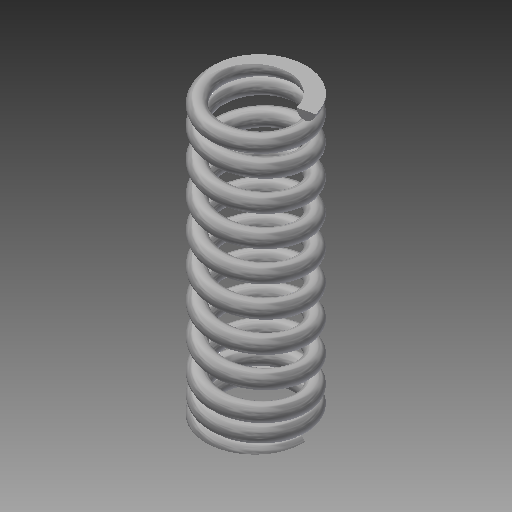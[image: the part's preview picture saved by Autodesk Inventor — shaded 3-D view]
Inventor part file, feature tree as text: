
AUTODESK INVENTOR PART (.ipt)
format: ipt  version: 2019 (Build 230136000, 136)  size: 1,027,072 bytes
history: native  units: mm
features: other x67, extrude x8, helix x5, sketch x3, sweep x2, plane x1
ambient origin geometry x8: Origin, YZ Plane, XZ Plane, XY Plane, X Axis, Y Axis, Z Axis, Center Point
bodies: Solid1 (feature_tree)
feature tree (86):
  other  "Main Coil Path(Right)"
  other  "Section Work Plane(Right)"
  other  "Start Work Plane(Right)"
  other  "End Work Plane(Right)"
  other  "End Cut Work Plane(Right)"
  other  "Start Cut Work Plane(Right)"
  other  "Plain Ends Cut Work Plane 1(Right)"
  other  "Plain Ends Cut Work Plane 2(Right)"
  sweep  "Main Coil Feature(R)"
  other  "Start Transition Coil 1(Right)"
  helix  "Coil  Start Transition 2(R)"  [1 undecoded]
  helix  "Coil  Start Transition 3(R)"  [1 undecoded]
  helix  "Coil  Start Transition 4(R)"  [1 undecoded]
  other  "Start Ends Coil(Right)"
  extrude  "Start Cut Feature(Right)"  Depth=10.0mm
  other  "End Transition Coil 1(Right)"
  other  "End Transition Coil 2(Right)"
  other  "End Transition Coil 3(Right)"
  other  "End Transition Coil 4(Right)"
  other  "End Coil(Right)"
  extrude  "End Cut Feature(Right)"  Depth=10.0mm
  extrude  "Plain Ends Cut Feature 1(Right)"  Depth=10.0mm
  extrude  "Plain Ends Cut  2(R)"  Depth=10.0mm TaperAngle=0.0deg
  other  "Main Coil Path(Left)"
  other  "Section Work Plane(Left)"
  other  "Start Work Plane(Left)"
  other  "End Work Plane(Left)"
  other  "End Cut Work Plane(Left)"
  other  "Start Cut Work Plane(Left)"
  other  "Plain Ends Cut Work Plane 1(Left)"
  other  "Plain Ends Cut Work Plane 2(Left)"
  sweep  "Main Coil Feature(L)"
  other  "Start Transition Coil 1(Left)"
  other  "Start Transition Coil 2(Left)"
  other  "Start Transition Coil 3(Left)"
  other  "Start Transition Coil 4(Left)"
  other  "Start Ends Coil(Left)"
  extrude  "Start Cut Feature(Left)"  Depth=10.0mm TaperAngle=0.0deg
  other  "End Transition Coil 1(Left)"
  other  "End Transition Coil 2(Left)"
  other  "End Transition Coil 3(Left)"
  other  "End Transition Coil 4(Left)"
  other  "End Coil(Left)"
  extrude  "End Cut Feature(Left)"  Depth=10.0mm
  extrude  "Cut Plain Ends Cut 1(L)"  Depth=10.0mm
  extrude  "Cut Plain Ends Cut 2(L)"  Depth=10.0mm
  other  "iMate Based Work Plane"
  other  "Preview Center Point"
  other  "Preview X Axis"
  other  "Path Section Sketch(Right)"
  other  "Srf1"
  helix  "Coil Section Sketch(Right)"  [1 undecoded]
  other  "Start Transition Coil Sketch 1(Right)"
  sketch  "Sketch  Start Transition 2(R)"  dims[d0=0.3mm d2=2.305084mm d3=10.0mm d4=67.124278mm]
  sketch  "Sketch  Start Transition 3(R)"  dims[d5=0.0mm d6=90.0deg d7=90.0deg d8=0.0mm d9=0.0mm d12=2.410832mm d13=-3.116461mm d14=1.2mm]
  sketch  "Sketch  Start Transition 4(R)"  dims[d15=0.0mm d16=2.028813mm d17=10.0mm d18=2.5mm d19=0.0mm d20=90.0deg d21=90.0deg d22=0.0mm d23=0.0mm d24=1.752542mm d25=10.0mm d26=2.5mm d27=0.0mm d28=90.0deg d29=90.0deg d30=0.0mm d31=0.0mm d32=1.476271mm d33=10.0mm d34=2.5mm d35=0.0mm d36=90.0deg d37=90.0deg d38=0.0mm d39=0.0mm d40=1.2mm d41=10.0mm d42=2.5mm d43=0.0mm d44=90.0deg d45=90.0deg d46=0.0mm d47=0.0mm d48=2.028813mm d49=10.0mm d50=1.875mm d51=0.0mm d52=90.0deg d53=90.0deg d54=0.0mm d55=0.0mm d56=1.752542mm d57=10.0mm d58=1.875mm d59=0.0mm d60=90.0deg d61=90.0deg d62=0.0mm d63=0.0mm d64=1.476271mm d65=10.0mm d66=1.875mm d67=0.0mm d68=90.0deg d69=90.0deg d70=0.0mm d71=0.0mm d72=1.2mm d73=10.0mm d74=1.875mm d75=0.0mm d76=90.0deg d77=90.0deg d78=0.0mm d79=0.0mm d81=10.0mm d82=15.0mm d83=0.0mm d84=90.0deg d85=90.0deg d86=0.0mm d87=0.0mm d88=1.208111mm d89=10.0mm d90=10.0mm d91=0.0mm d92=90.0deg d93=90.0deg d94=0.0mm d95=0.0mm d96=7.5mm d97=1.208111mm d98=0.0mm d99=7.5mm d100=1.208111mm d101=0.0mm d102=0.0mm d103=10.0mm d104=10.0mm d105=10.0mm d106=10.0mm d108=10.0mm d112=10.0mm d113=10.0mm d114=10.0mm d121=0.310112mm d131=10.0mm d132=10.0mm d133=10.0mm d134=10.0mm d135=0.3mm d137=2.305084mm d138=10.0mm d139=67.124278mm d140=0.0mm d141=90.0deg d142=90.0deg d143=0.0mm d144=0.0mm d145=2.410832mm d146=-3.116461mm d147=0.310112mm d148=0.008084mm d149=1.2mm d150=0.0mm d151=0.0mm d152=2.028813mm d153=10.0mm d154=2.5mm d155=0.0mm d156=90.0deg d157=90.0deg d158=0.0mm d159=0.0mm d160=1.752542mm d161=10.0mm d162=2.5mm d163=0.0mm d164=90.0deg d165=90.0deg d166=0.0mm d167=0.0mm d168=1.476271mm d169=10.0mm d170=2.5mm d171=0.0mm d172=90.0deg d173=90.0deg d174=0.0mm d175=0.0mm d176=1.2mm d177=10.0mm d178=2.5mm d179=0.0mm d180=90.0deg d181=90.0deg d182=0.0mm d183=0.0mm d184=0.0mm d185=0.0mm d186=0.0mm d187=0.0mm d188=1.208111mm d189=10.0mm d190=15.0mm d191=0.0mm d192=90.0deg d193=90.0deg d194=0.0mm d195=0.0mm d196=0.0mm d197=7.5mm d198=1.208111mm d199=0.0mm d200=0.0mm d201=2.028813mm d202=10.0mm d203=1.875mm d204=0.0mm d205=90.0deg d206=90.0deg d207=0.0mm d208=0.0mm d209=0.0mm d210=1.752542mm d211=10.0mm d212=1.875mm d213=0.0mm d214=90.0deg d215=90.0deg d216=0.0mm d217=0.0mm d218=1.476271mm d219=10.0mm d220=1.875mm d221=0.0mm d222=90.0deg d223=90.0deg d224=0.0mm d225=0.0mm d226=1.2mm d227=10.0mm d228=1.875mm d229=0.0mm d230=90.0deg d231=90.0deg d232=0.0mm d233=0.0mm d234=0.0mm d235=0.0mm d236=0.0mm d237=1.208111mm d238=10.0mm d239=10.0mm d240=0.0mm d241=90.0deg d242=90.0deg d243=0.0mm d244=0.0mm d245=7.5mm d246=1.208111mm d247=0.0mm d248=0.0mm d249=0.0mm d254=7.5mm d255=10.0mm d256=0.0mm d257=10.0mm d258=-0.008084mm d259=7.5mm d260=10.0mm d261=0.0mm d262=20.0mm d263=7.5mm d264=10.0mm d265=0.0mm d266=20.0mm d267=0.0mm d270=-2.966461mm d271=0.0mm d272=7.5mm d273=10.0mm d274=0.0mm d275=10.0mm d276=157.079633mm d277=6.3mm d278=6.3mm d279=0.0mm d280=0.0mm]
  other  "End Transition Coil Sketch 1(Right)"
  other  "End Transition Coil Sketch 2(Right)"
  other  "End Transition Coil Sketch 3(Right)"
  other  "End Transition Coil Sketch 4(Right)"
  other  "Start Ends Skecth(Right)"
  other  "End Coil Skecth(Right)"
  other  "End Cut Sketch(Right)"
  other  "Start Cut Sketch(Right)"
  other  "Path Section Sketch(Left)"
  other  "Srf2"
  helix  "Coil Section Sketch(Left)"  [1 undecoded]
  other  "Start Transition Coil Sketch 1(Left)"
  other  "Start Transition Coil Sketch 2(Left)"
  other  "Start Transition Coil Sketch 3(Left)"
  other  "Start Transition Coil Sketch 4(Left)"
  other  "Start Ends Skecth(Left)"
  other  "Start Cut Sketch(Left)"
  other  "End Transition Coil Sketch 1(Left)"
  other  "End Transition Coil Sketch 2(Left)"
  other  "End Transition Coil Sketch 3(Left)"
  other  "End Transition Coil Sketch 4(Left)"
  other  "End Coil Skecth(Left)"
  other  "End Cut Sketch(Left)"
  other  "Plain Ends Cut Sketch 2(Left)"
  other  "Plain Ends Cut Sketch 2(Right)"
  other  "Plain Ends Cut Sketch 1(Right)"
  other  "Plain Ends Cut Sketch 1(Left)"
  plane  "Work Plane Start Section"
  other  "Basic Curve(Right)"
  other  "Basic Curve(Left)"
note: 5 required parameter values undecoded (feature->parameter linkage not recoverable at this tier; creation-order binding heuristic only, values carry confidence <= 0.55)
